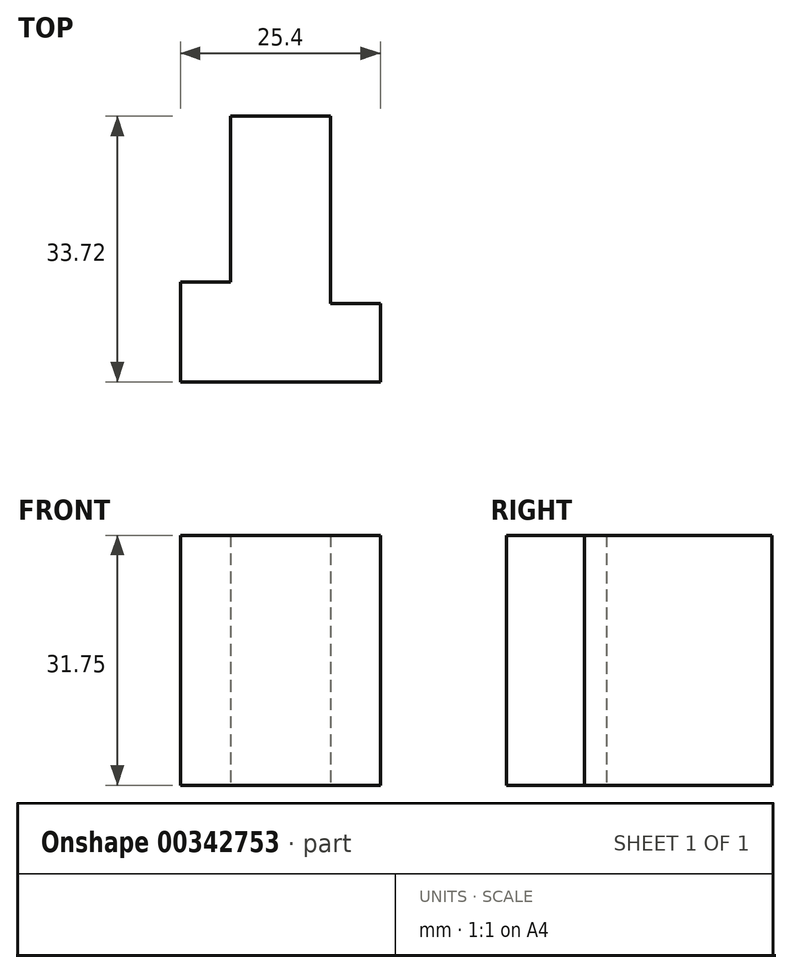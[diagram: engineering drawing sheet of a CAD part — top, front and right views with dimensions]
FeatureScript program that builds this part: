
annotation { "Feature Type Name" : "Feature", "Feature Type Description" : "" }
export const myFeature = defineFeature(function(context is Context, id is Id, definition is map)
    precondition{}
    {
        {
            var Q0;
            Q0=qCreatedBy(makeId("Top.planeOp"),FACE);
            var sketch = newSketch(context, id + "F0", { "sketchPlane" : qUnion([Q0])});
            skLineSegment(sketch, "E0", {"start": v(0, 0) * mm, "end": v(-25.4, 0) * mm});
            skLineSegment(sketch, "E1", {"start": v(-25.4, 0) * mm, "end": v(-25.4, 12.7) * mm});
            skLineSegment(sketch, "E2", {"start": v(-25.4, 12.7) * mm, "end": v(-19.05, 12.7) * mm});
            skLineSegment(sketch, "E3", {"start": v(-19.05, 12.7) * mm, "end": v(-19.05, 33.72) * mm});
            skLineSegment(sketch, "E4", {"start": v(-19.05, 33.72) * mm, "end": v(-6.35, 33.72) * mm});
            skLineSegment(sketch, "E5", {"start": v(-6.35, 33.72) * mm, "end": v(-6.35, 9.93) * mm});
            skLineSegment(sketch, "E6", {"start": v(-6.35, 9.93) * mm, "end": v(0, 9.93) * mm});
            skLineSegment(sketch, "E7", {"start": v(0, 9.93) * mm, "end": v(0, 0) * mm});
            skSolve(sketch);
        }
        {
            var Q0;
            Q0=makeQuery(id+"F0.imprint","IMPRINT",FACE,{"disambiguationData":[TD([[makeQuery(id+"F0.imprint","IMPRINT",EDGE,{"derivedFrom":sQuery(id+"F0.wireOp",EDGE,"E0")}),-1.0]])]});
            extrude(context, id + "F1", {"entities" : qUnion([Q0]), "depth" : 31.75 * mm});
        }
    });
